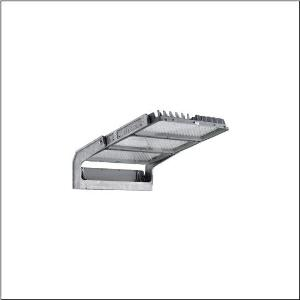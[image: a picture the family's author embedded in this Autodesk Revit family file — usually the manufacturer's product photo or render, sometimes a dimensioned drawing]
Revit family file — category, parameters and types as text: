
# Revit family: floodlight_fl_11_maxi_pro___rs08_5xa779228l01gb_a1ed
name_source: partatom
category: Lighting Fixtures
units: mm (PartAtom-declared; Revit-internal decimal feet)

## family parameters
Cut with Voids When Loaded = No
Host = Face
Light Source = No
Part Type = Normal
Room Calculation Point = No
Round Connector Dimension = Use Diameter
Shared = No

## types (1)
- --- (1 x LED, 148170 lm, 1285.1 W, 5700K)
    Apparent Load = 1285 VA
    CIE Flux Codes = 70 87 98 100 100
    Color Rendering = 80
    Color Temperature = 5700K
    Default Elevation = 1800 mm
    Description = Floodlight FL 11  maxi  pro floodlight; light control with lens of PMMA; cover panel of toughened safety glass, transparent; light distribution: RS08, rotationally symmetric direct distribution, LED; colour temperature: 5700K, rated luminous flux: 148.170lm, colour rendering: CRI > 80, light colour: 857; luminous efficacy: 115lm/W; brightness control: DMX+RDM; with terminal, 6-pole, max. 2.5mm², mains connection: 220..240V/380..400V AC, 50/60Hz, surge voltage resistance: line to ground: 10kV, LED service life up to 100,000h L90. Typical operating time: 1000h per year., ECG replaceable separately, LED unit replaceable without ESD environment, dustproof LED module, dimming range 10..100%; 1285W floodlight with 3x LED unit of diecast aluminium, coated grey; length: 1.003mm / width: 651mm / height: 338mm; mounting bracket, of diecast aluminium, uncoated, natural, equipment: Power, protection rating (complete): IP66; insulation class (complete): insulation class I (protective earthing); certification: CE, ENEC, VDE; ball protection: ball impact resistant, only for outdoor installations in the designated locations, permissible operating ambient temperature: -45..+55°C, permissible storage temperature: -40..+85°Cpackaging unit: 1 piece

Light Distribution: RS08
    Height = 320 mm
    Lamp = 1 x LED
    Lamp Light Flux = 148170 lm
    Lamp Power = 1285.1 W
    Lamp count = 1
    Length = 1002 mm
    Luminous efficacy = 115 lm/W
    Manufacturer = Siteco
    ModVariant = No
    Model = 5XA779228L01GB
    Mounting Place = Ceiling
    Mounting Type = Surface mounted
    Number of Poles = 1
    OnlyDefault = Yes
    Power Factor = 1
    Product Name = Floodlight FL 11 maxi pro | RS08
    Product group = floodlight | ceiling mounted
    ProductGroupID = 303
    Protection Class = Protection class I
    Protection Degree = IP 66
    RLX_Detail_Level = 1
    RLX_Emergency_Light_Flux = 0 lm
    RLX_Emergency_Type = 0
    RLX_Emergency_Type_DB = No
    RlxData = <blob elided: 40313 chars, md5=56dbb032>
    Socket = socket
    Standby Power = 0 W
    System Light Flux = 148170 lm
    System Power = 1285 W
    Type Comments = factory setting: luminous flux: 100 % | dim-lin: 255 | 875 mA
    Type Image = l_1356210.jpg
    URL = http://relux.com
    VarID = @adj_033719
    Voltage = 0 V
    Weight = 0.00 kg
    Width = 655 mm

## geometry (parser evidence)
native form markers: Blend x4, Sweep x12
no freeform markers — native parametric forms only
